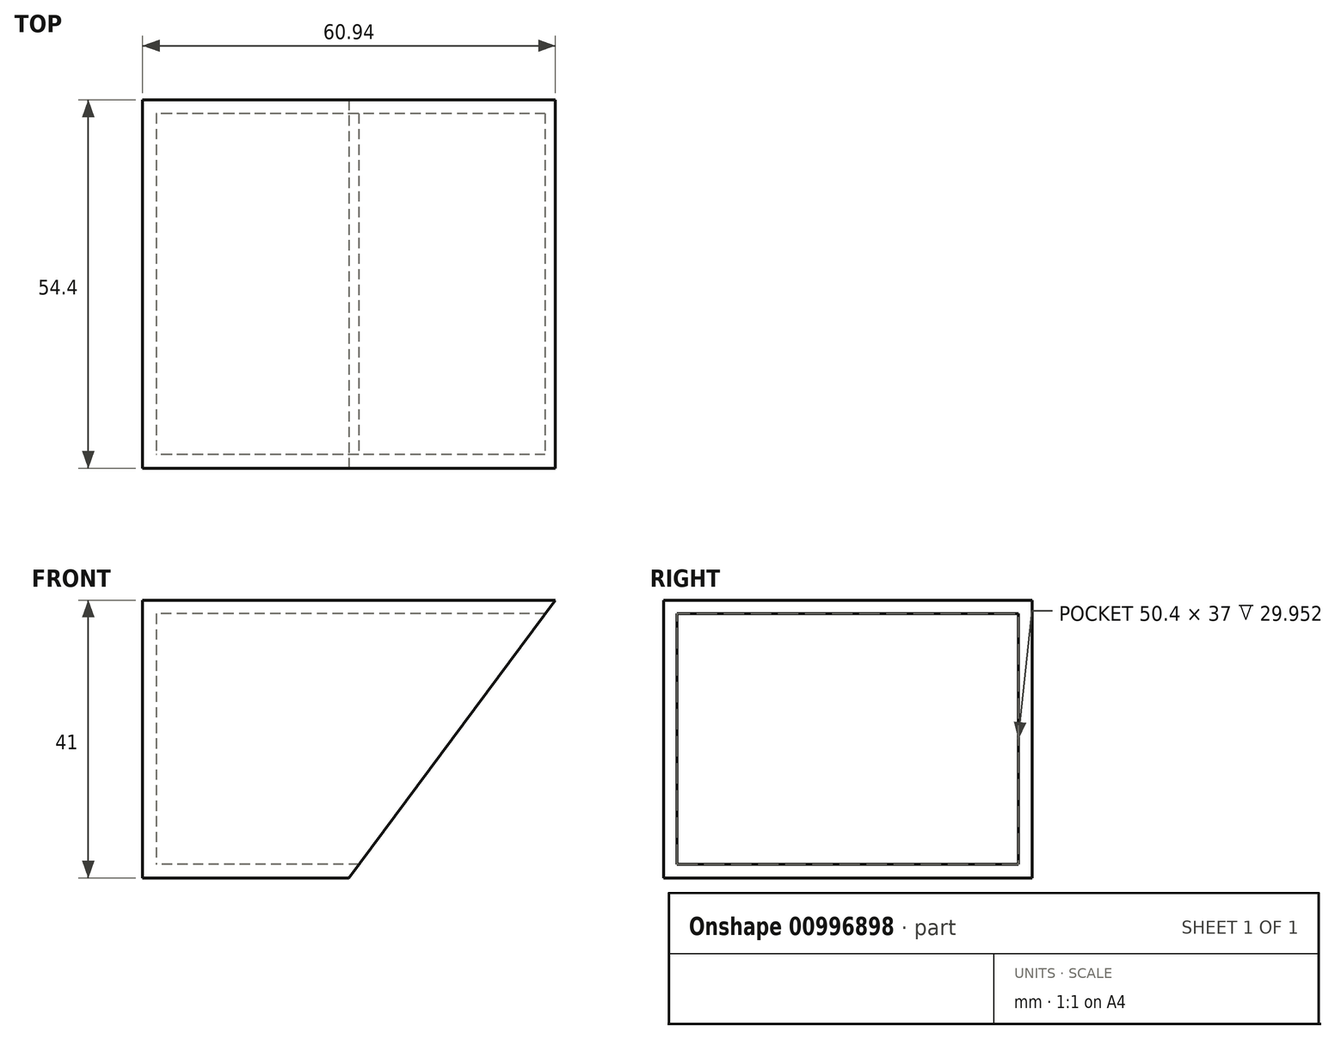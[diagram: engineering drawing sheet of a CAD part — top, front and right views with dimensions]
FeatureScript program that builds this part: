
annotation { "Feature Type Name" : "Feature", "Feature Type Description" : "" }
export const myFeature = defineFeature(function(context is Context, id is Id, definition is map)
    precondition{}
    {
        {
            var Q0;
            Q0=qCreatedBy(makeId("Top.planeOp"),FACE);
            var sketch = newSketch(context, id + "F0", { "sketchPlane" : qUnion([Q0])});
            skLineSegment(sketch, "E0.bottom", {"start": v(28.47, 25.2) * mm, "end": v(-28.47, 25.2) * mm});
            skLineSegment(sketch, "E0.top", {"start": v(28.47, -25.2) * mm, "end": v(-28.47, -25.2) * mm});
            skLineSegment(sketch, "E0.left", {"start": v(28.47, 25.2) * mm, "end": v(28.47, -25.2) * mm});
            skLineSegment(sketch, "E0.right", {"start": v(-28.47, 25.2) * mm, "end": v(-28.47, -25.2) * mm});
            skPoint(sketch, "E0.middle", {"position": v(0, 0) * mm});
            skLineSegment(sketch, "E1.0", {"start": v(30.47, -27.2) * mm, "end": v(-30.47, -27.2) * mm});
            skLineSegment(sketch, "E1.1", {"start": v(30.47, 27.2) * mm, "end": v(30.47, -27.2) * mm});
            skLineSegment(sketch, "E1.2", {"start": v(30.47, 27.2) * mm, "end": v(-30.47, 27.2) * mm});
            skLineSegment(sketch, "E1.3", {"start": v(-30.47, 27.2) * mm, "end": v(-30.47, -27.2) * mm});
            skSolve(sketch);
        }
        {
            var Q0;
            Q0=makeQuery(id+"F0.imprint","IMPRINT",FACE,{"disambiguationData":[TD([[makeQuery(id+"F0.imprint","IMPRINT",EDGE,{"derivedFrom":sQuery(id+"F0.wireOp",EDGE,"E0.bottom")}),-1.0]])]});
            var Q1;
            Q1=makeQuery(id+"F0.imprint","IMPRINT",FACE,{"disambiguationData":[TD([[makeQuery(id+"F0.imprint","IMPRINT",EDGE,{"derivedFrom":sQuery(id+"F0.wireOp",EDGE,"E0.bottom")}),1.0]])]});
            extrude(context, id + "F1", {"entities" : qUnion([Q0, Q1]), "depth" : 41 * mm, "offsetDistance" : 25 * mm});
        }
        {
            var Q0;
            Q0=makeQuery(id+"F1.opExtrude","SWEPT_FACE",FACE,{"disambiguationData":[OSD([sQuery(id+"F0.wireOp",EDGE,"E1.0")])]});
            var sketch = newSketch(context, id + "F2", { "sketchPlane" : qUnion([Q0])});
            skLineSegment(sketch, "E2", {"start": v(30.47, 41) * mm, "end": v(0, 0) * mm});
            skSolve(sketch);
        }
        {
            var Q0;
            {var subQ0=sQuery(id+"F2.wireOp",EDGE,"E2");Q0=makeQuery(id+"F2.imprint","IMPRINT",FACE,{"disambiguationData":[TD([[makeQuery(id+"F2.imprint","IMPRINT",EDGE,{"derivedFrom":subQ0}),1.0]])]});}
            extrude(context, id + "F3", {"entities" : qUnion([Q0]), "operationType" : NewBodyOperationType.REMOVE, "endBound" : BoundingType.THROUGH_ALL, "oppositeDirection" : true, "depth" : 25 * mm, "offsetDistance" : 25 * mm});
        }
        {
            var Q0;
            Q0=makeQuery(id+"F3.boolean.opBoolean","COPY",FACE,{"derivedFrom":makeQuery(id+"F3.opExtrude","SWEPT_FACE",FACE,{"disambiguationData":[OSD([sQuery(id+"F2.wireOp",EDGE,"E2")])]})});
            shell(context, id + "F4", {"entities" : qUnion([Q0]), "thickness" : 2 * mm});
        }
    });
